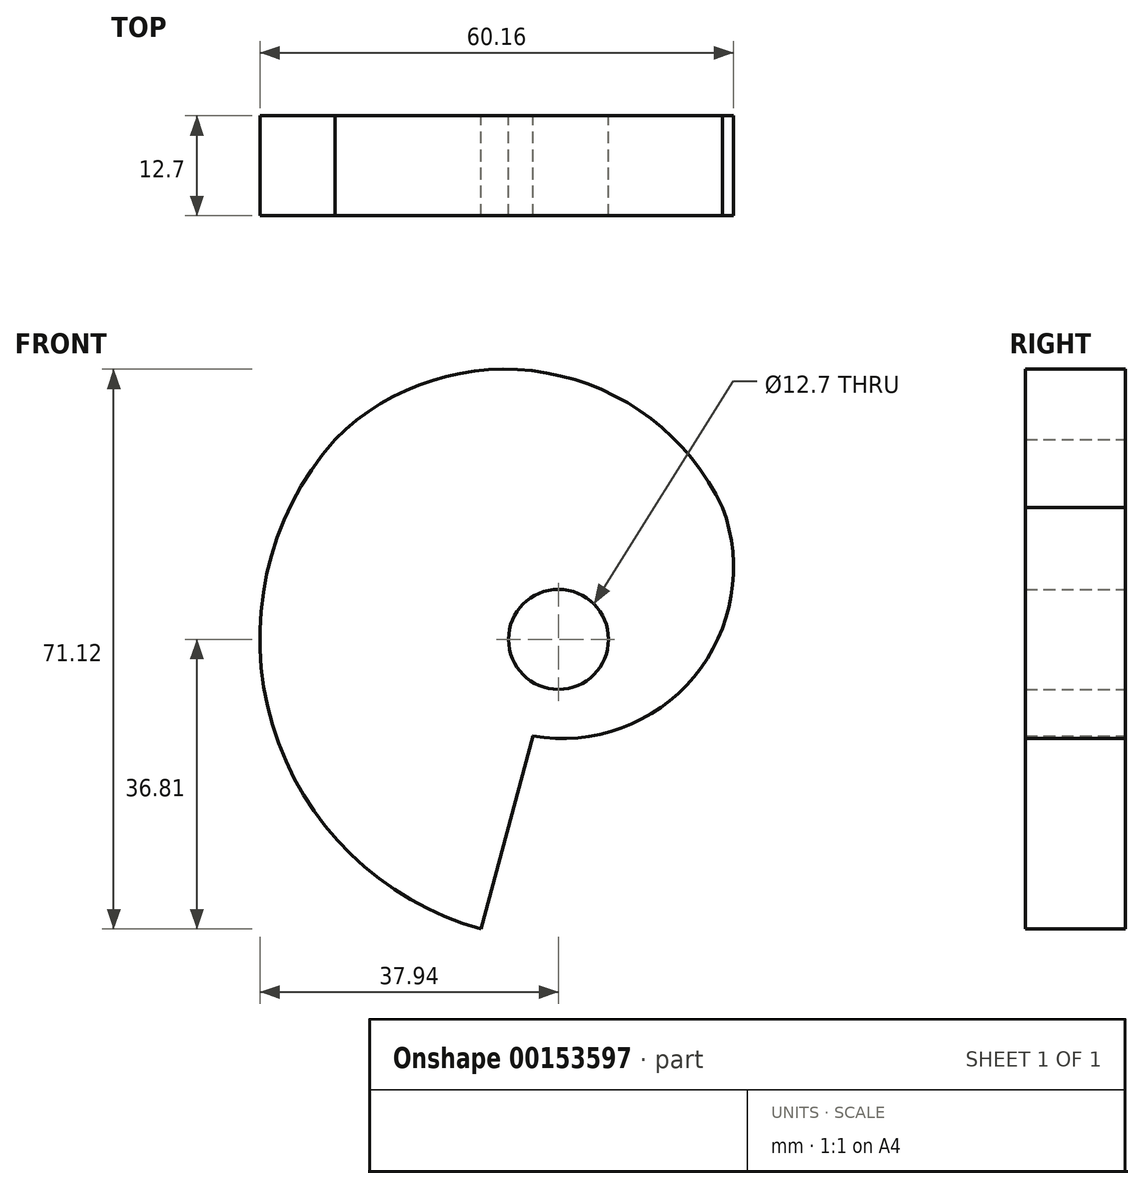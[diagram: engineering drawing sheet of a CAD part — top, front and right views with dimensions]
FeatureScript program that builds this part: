
annotation { "Feature Type Name" : "Feature", "Feature Type Description" : "" }
export const myFeature = defineFeature(function(context is Context, id is Id, definition is map)
    precondition{}
    {
        {
            var Q0;
            Q0=qCreatedBy(makeId("Front.planeOp"),FACE);
            var sketch = newSketch(context, id + "F0", { "sketchPlane" : qUnion([Q0])});
            skCircle(sketch, "E0", {"center": v(0, 0) * mm, "radius": 38.1 * mm, "construction": true});
            skLineSegment(sketch, "E1", {"start": v(-9.82, -36.81) * mm, "end": v(-3.27, -12.27) * mm});
            skArc(sketch, "E2", {"start": v(-28.4, 25.4) * mm, "mid": v(-36.34, -10.86) * mm, "end": v(-9.82, -36.81) * mm});
            skArc(sketch, "E3", {"start": v(20.84, 16.74) * mm, "mid": v(-1.54, 33.85) * mm, "end": v(-28.4, 25.4) * mm});
            skArc(sketch, "E4", {"start": v(-3.27, -12.27) * mm, "mid": v(17.21, -4.77) * mm, "end": v(20.84, 16.74) * mm});
            skSolve(sketch);
        }
        {
            var Q0;
            Q0=makeQuery(id+"F0.imprint","IMPRINT",FACE,{"disambiguationData":[TD([[makeQuery(id+"F0.imprint","IMPRINT",EDGE,{"derivedFrom":sQuery(id+"F0.wireOp",EDGE,"E1")}),1.0]])]});
            var sketch = newSketch(context, id + "F1", { "sketchPlane" : qUnion([Q0])});
            skCircle(sketch, "E5", {"center": v(0, 0) * mm, "radius": 6.35 * mm});
            skSolve(sketch);
        }
        {
            var Q0;
            Q0=qSketchRegion(id+"F0",true);
            extrude(context, id + "F2", {"entities" : qUnion([Q0]), "depth" : 12.7 * mm});
        }
        {
            var Q0;
            Q0=qSketchRegion(id+"F1",true);
            extrude(context, id + "F3", {"entities" : qUnion([Q0]), "operationType" : NewBodyOperationType.REMOVE, "depth" : 25.4 * mm});
        }
    });
